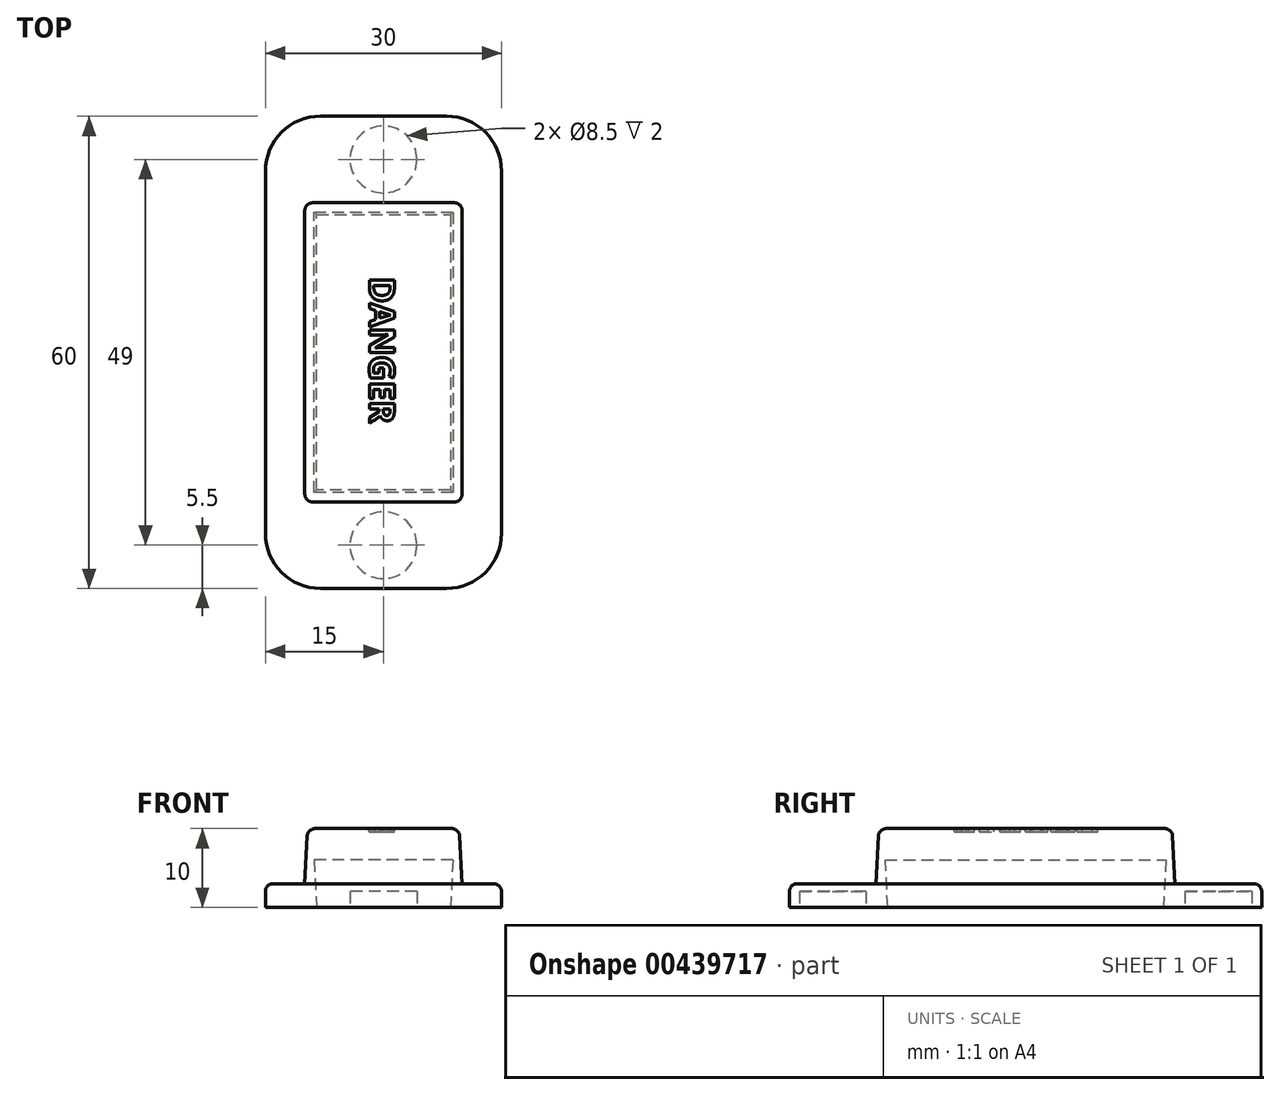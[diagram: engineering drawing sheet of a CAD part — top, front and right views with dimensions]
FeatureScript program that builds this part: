
annotation { "Feature Type Name" : "Feature", "Feature Type Description" : "" }
export const myFeature = defineFeature(function(context is Context, id is Id, definition is map)
    precondition{}
    {
        {
            var Q0;
            Q0=qCreatedBy(makeId("Top.planeOp"),FACE);
            var sketch = newSketch(context, id + "F0", { "sketchPlane" : qUnion([Q0])});
            skLineSegment(sketch, "E0.bottom", {"start": v(-15, 30) * mm, "end": v(15, 30) * mm});
            skLineSegment(sketch, "E0.top", {"start": v(-15, -30) * mm, "end": v(15, -30) * mm});
            skLineSegment(sketch, "E0.left", {"start": v(-15, 30) * mm, "end": v(-15, -30) * mm});
            skLineSegment(sketch, "E0.right", {"start": v(15, 30) * mm, "end": v(15, -30) * mm});
            skSolve(sketch);
        }
        {
            var Q0;
            Q0=makeQuery(id+"F0.imprint","IMPRINT",FACE,{"disambiguationData":[TD([[makeQuery(id+"F0.imprint","IMPRINT",EDGE,{"derivedFrom":sQuery(id+"F0.wireOp",EDGE,"E0.bottom")}),-1.0]])]});
            extrude(context, id + "F1", {"entities" : qUnion([Q0]), "depth" : 3 * mm});
        }
        {
            var Q0;
            Q0=makeQuery(id+"F1.opExtrude","CAP_FACE",FACE,{"disambiguationData":[OSD([sQuery(id+"F0.wireOp",EDGE,"E0.bottom"),sQuery(id+"F0.wireOp",EDGE,"E0.top"),sQuery(id+"F0.wireOp",EDGE,"E0.left"),sQuery(id+"F0.wireOp",EDGE,"E0.right")])],"isStart":false});
            var sketch = newSketch(context, id + "F2", { "sketchPlane" : qUnion([Q0])});
            skLineSegment(sketch, "E1.bottom", {"start": v(-10, 19) * mm, "end": v(10, 19) * mm});
            skLineSegment(sketch, "E1.top", {"start": v(-10, -19) * mm, "end": v(10, -19) * mm});
            skLineSegment(sketch, "E1.left", {"start": v(-10, 19) * mm, "end": v(-10, -19) * mm});
            skLineSegment(sketch, "E1.right", {"start": v(10, 19) * mm, "end": v(10, -19) * mm});
            skPoint(sketch, "E1.middle", {"position": v(0, 0) * mm});
            skSolve(sketch);
        }
        {
            var Q0;
            Q0=makeQuery(id+"F2.imprint","IMPRINT",FACE,{"disambiguationData":[TD([[makeQuery(id+"F2.imprint","IMPRINT",EDGE,{"derivedFrom":sQuery(id+"F2.wireOp",EDGE,"E1.bottom")}),-1.0]])]});
            extrude(context, id + "F3", {"entities" : qUnion([Q0]), "operationType" : NewBodyOperationType.ADD, "depth" : 7 * mm, "hasDraft" : true, "draftAngle" : 3 * degree, "draftPullDirection" : true});
        }
        {
            var Q0;
            Q0=makeQuery(id+"F0.imprint","IMPRINT",FACE,{"disambiguationData":[TD([[makeQuery(id+"F0.imprint","IMPRINT",EDGE,{"derivedFrom":sQuery(id+"F0.wireOp",EDGE,"E0.bottom")}),-1.0]])]});
            var sketch = newSketch(context, id + "F4", { "sketchPlane" : qUnion([Q0])});
            skLineSegment(sketch, "E2.bottom", {"start": v(-8.5, -17.5) * mm, "end": v(8.5, -17.5) * mm});
            skLineSegment(sketch, "E2.top", {"start": v(-8.5, 17.5) * mm, "end": v(8.5, 17.5) * mm});
            skLineSegment(sketch, "E2.left", {"start": v(-8.5, -17.5) * mm, "end": v(-8.5, 17.5) * mm});
            skLineSegment(sketch, "E2.right", {"start": v(8.5, -17.5) * mm, "end": v(8.5, 17.5) * mm});
            skPoint(sketch, "E2.middle", {"position": v(0, 0) * mm});
            skSolve(sketch);
        }
        {
            var Q0;
            Q0=makeQuery(id+"F0.imprint","IMPRINT",FACE,{"disambiguationData":[TD([[makeQuery(id+"F0.imprint","IMPRINT",EDGE,{"derivedFrom":sQuery(id+"F0.wireOp",EDGE,"E0.bottom")}),-1.0]])]});
            var sketch = newSketch(context, id + "F5", { "sketchPlane" : qUnion([Q0])});
            skCircle(sketch, "E3", {"center": v(0, -24.5) * mm, "radius": 4.25 * mm});
            skCircle(sketch, "E4.0.1.0", {"center": v(0, 24.5) * mm, "radius": 4.25 * mm});
            skLineSegment(sketch, "E4.direction2", {"start": v(0, -24.5) * mm, "end": v(0, 24.5) * mm, "construction": true});
            skSolve(sketch);
        }
        {
            var Q0;
            Q0=makeQuery(id+"F4.imprint","IMPRINT",FACE,{"disambiguationData":[TD([[makeQuery(id+"F4.imprint","IMPRINT",EDGE,{"derivedFrom":sQuery(id+"F4.wireOp",EDGE,"E2.bottom")}),1.0]])]});
            extrude(context, id + "F6", {"entities" : qUnion([Q0]), "operationType" : NewBodyOperationType.REMOVE, "depth" : 6 * mm, "hasDraft" : true, "draftAngle" : 3 * degree});
        }
        {
            var Q0;
            Q0=makeQuery(id+"F5.imprint","IMPRINT",FACE,{"disambiguationData":[TD([[makeQuery(id+"F5.imprint","IMPRINT",EDGE,{"derivedFrom":sQuery(id+"F5.wireOp",EDGE,"E3")}),1.0]])]});
            var Q1;
            Q1=makeQuery(id+"F5.imprint","IMPRINT",FACE,{"disambiguationData":[TD([[makeQuery(id+"F5.imprint","IMPRINT",EDGE,{"derivedFrom":sQuery(id+"F5.wireOp",EDGE,"E4.0.1.0")}),1.0]])]});
            extrude(context, id + "F7", {"entities" : qUnion([Q0, Q1]), "operationType" : NewBodyOperationType.REMOVE, "depth" : 2 * mm});
        }
        {
            var Q0;
            Q0=makeQuery(id+"F3.opExtrude","CAP_FACE",FACE,{"disambiguationData":[OSD([sQuery(id+"F2.wireOp",EDGE,"E1.bottom"),sQuery(id+"F2.wireOp",EDGE,"E1.top"),sQuery(id+"F2.wireOp",EDGE,"E1.left"),sQuery(id+"F2.wireOp",EDGE,"E1.right")])],"isStart":false});
            var sketch = newSketch(context, id + "F8", { "sketchPlane" : qUnion([Q0])});
            skText(sketch, "E5", { "text": "DANGER", "fontName": "OpenSans-Bold.ttf"});
            const initialGuessF8  = {"E5": [-0.00179, 0.00957, 0, -1, 0.0032]};
            skSetInitialGuess(sketch, initialGuessF8);
            skSolve(sketch);
        }
        {
            var Q0;
            Q0 = qSketchRegion(id + "F8", true);
            extrude(context, id + "F9", {"entities" : qUnion([Q0]), "operationType" : NewBodyOperationType.REMOVE, "oppositeDirection" : true, "depth" : 0.4 * mm});
        }
        {
            var Q0;
            Q0=makeQuery(id+"F1.opExtrude","SWEPT_EDGE",EDGE,{"disambiguationData":[OSD([sQuery(id+"F0.wireOp",EDGE,"E0.bottom"),sQuery(id+"F0.wireOp",EDGE,"E0.left")])]});
            var Q1;
            Q1=makeQuery(id+"F1.opExtrude","SWEPT_EDGE",EDGE,{"disambiguationData":[OSD([sQuery(id+"F0.wireOp",EDGE,"E0.bottom"),sQuery(id+"F0.wireOp",EDGE,"E0.right")])]});
            var Q2;
            Q2=makeQuery(id+"F1.opExtrude","SWEPT_EDGE",EDGE,{"disambiguationData":[OSD([sQuery(id+"F0.wireOp",EDGE,"E0.top"),sQuery(id+"F0.wireOp",EDGE,"E0.left")])]});
            var Q3;
            Q3=makeQuery(id+"F1.opExtrude","SWEPT_EDGE",EDGE,{"disambiguationData":[OSD([sQuery(id+"F0.wireOp",EDGE,"E0.top"),sQuery(id+"F0.wireOp",EDGE,"E0.right")])]});
            fillet(context, id + "F10", {"entities" : qUnion([Q0, Q1, Q2, Q3]), "radius" : 7 * mm, "tangentPropagation" : true, "allowEdgeOverflow" : false});
        }
        {
            var Q0;
            Q0=makeQuery(id+"F3.opExtrude","SWEPT_EDGE",EDGE,{"disambiguationData":[OSD([sQuery(id+"F2.wireOp",EDGE,"E1.bottom"),sQuery(id+"F2.wireOp",EDGE,"E1.left")])]});
            var Q1;
            Q1=makeQuery(id+"F3.opExtrude","SWEPT_EDGE",EDGE,{"disambiguationData":[OSD([sQuery(id+"F2.wireOp",EDGE,"E1.top"),sQuery(id+"F2.wireOp",EDGE,"E1.left")])]});
            var Q2;
            Q2=makeQuery(id+"F3.opExtrude","SWEPT_EDGE",EDGE,{"disambiguationData":[OSD([sQuery(id+"F2.wireOp",EDGE,"E1.top"),sQuery(id+"F2.wireOp",EDGE,"E1.right")])]});
            var Q3;
            Q3=makeQuery(id+"F3.opExtrude","SWEPT_EDGE",EDGE,{"disambiguationData":[OSD([sQuery(id+"F2.wireOp",EDGE,"E1.bottom"),sQuery(id+"F2.wireOp",EDGE,"E1.right")])]});
            var Q4;
            Q4=makeQuery(id+"F3.opExtrude","CAP_EDGE",EDGE,{"disambiguationData":[OSD([sQuery(id+"F2.wireOp",EDGE,"E1.right")])],"isStart":false});
            var Q5;
            Q5=makeQuery(id+"F3.opExtrude","CAP_EDGE",EDGE,{"disambiguationData":[OSD([sQuery(id+"F2.wireOp",EDGE,"E1.top")])],"isStart":false});
            var Q6;
            Q6=makeQuery(id+"F3.opExtrude","CAP_EDGE",EDGE,{"disambiguationData":[OSD([sQuery(id+"F2.wireOp",EDGE,"E1.left")])],"isStart":false});
            var Q7;
            Q7=makeQuery(id+"F3.opExtrude","CAP_EDGE",EDGE,{"disambiguationData":[OSD([sQuery(id+"F2.wireOp",EDGE,"E1.bottom")])],"isStart":false});
            var Q8;
            Q8=makeQuery(id+"F3.opExtrude","CAP_EDGE",EDGE,{"disambiguationData":[OSD([sQuery(id+"F2.wireOp",EDGE,"E1.left")])],"isStart":true});
            var Q9;
            Q9=makeQuery(id+"F1.opExtrude","CAP_EDGE",EDGE,{"disambiguationData":[OSD([sQuery(id+"F0.wireOp",EDGE,"E0.left")])],"isStart":false});
            fillet(context, id + "F11", {"entities" : qUnion([Q0, Q1, Q2, Q3, Q4, Q5, Q6, Q7, Q8, Q9]), "radius" : 1 * mm, "tangentPropagation" : true, "allowEdgeOverflow" : false});
        }
    });
